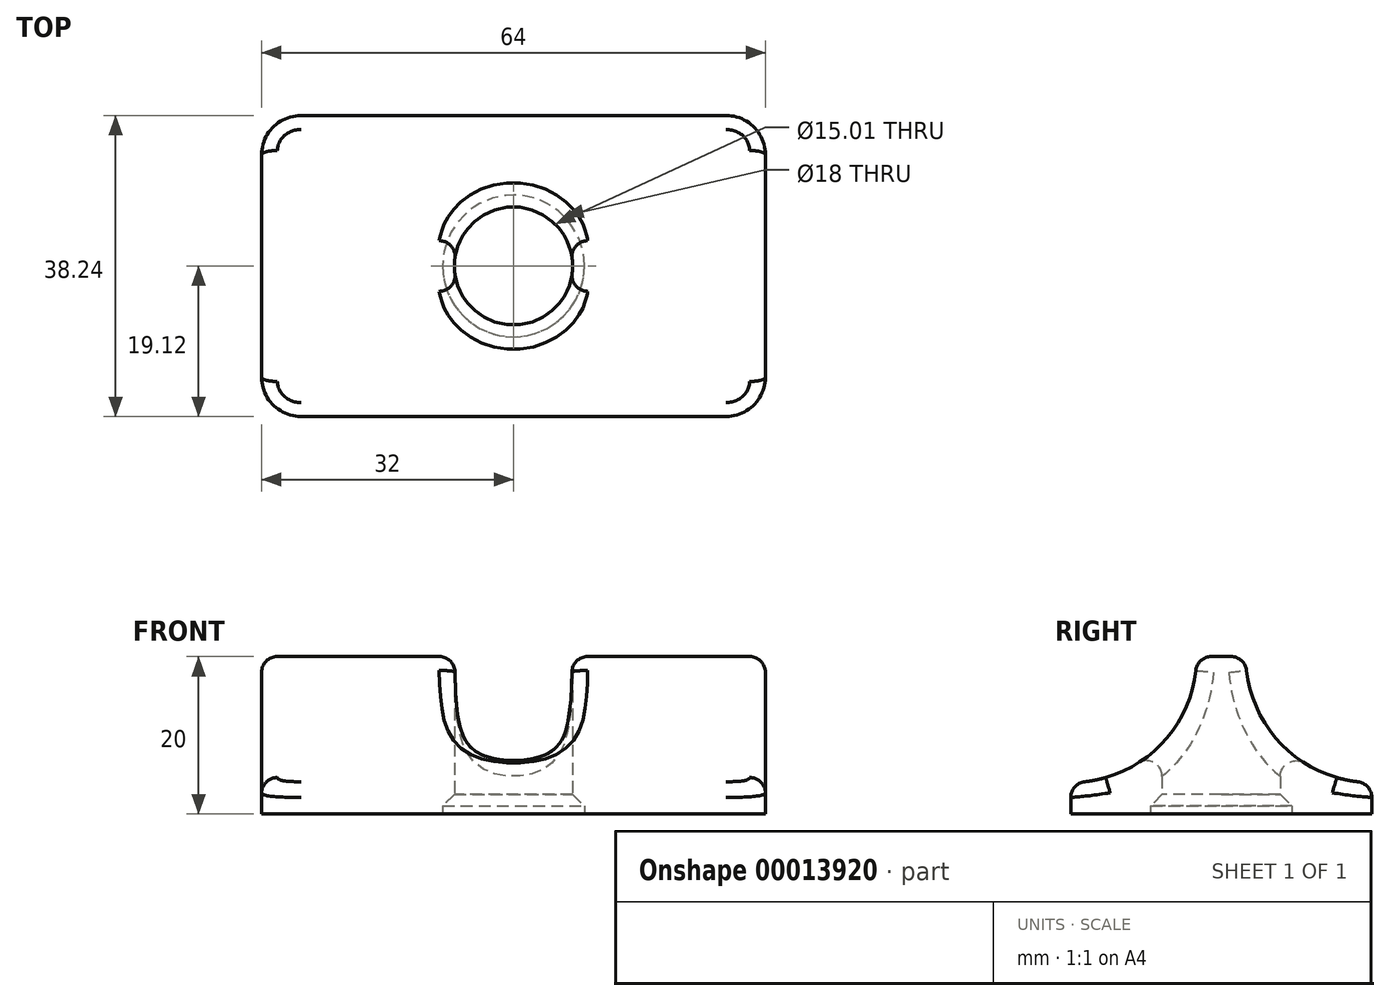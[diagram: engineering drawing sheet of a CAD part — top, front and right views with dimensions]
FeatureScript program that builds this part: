
annotation { "Feature Type Name" : "Feature", "Feature Type Description" : "" }
export const myFeature = defineFeature(function(context is Context, id is Id, definition is map)
    precondition{}
    {
        {
            var Q0;
            Q0=qCreatedBy(makeId("Right.planeOp"),FACE);
            var sketch = newSketch(context, id + "F0", { "sketchPlane" : qUnion([Q0])});
            skLineSegment(sketch, "E0", {"start": v(-19.12, 0) * mm, "end": v(19.12, 0) * mm});
            skArc(sketch, "E1", {"start": v(3.12, 20) * mm, "mid": v(7.8, 8.69) * mm, "end": v(19.12, 4) * mm});
            skArc(sketch, "E2", {"start": v(-19.12, 4) * mm, "mid": v(-7.8, 8.69) * mm, "end": v(-3.12, 20) * mm});
            skLineSegment(sketch, "E3", {"start": v(-19.12, 0) * mm, "end": v(-19.12, 4) * mm});
            skLineSegment(sketch, "E4", {"start": v(19.12, 0) * mm, "end": v(19.12, 4) * mm});
            skLineSegment(sketch, "E5", {"start": v(-7.5, 0) * mm, "end": v(-7.5, 9) * mm, "construction": true});
            skLineSegment(sketch, "E6", {"start": v(-7.5, 9) * mm, "end": v(7.5, 9) * mm, "construction": true});
            skLineSegment(sketch, "E7", {"start": v(7.5, 9) * mm, "end": v(7.5, 0) * mm, "construction": true});
            skLineSegment(sketch, "E8", {"start": v(0, 9) * mm, "end": v(0, 0) * mm, "construction": true});
            skLineSegment(sketch, "E9", {"start": v(-3.12, 20) * mm, "end": v(3.12, 20) * mm});
            skSolve(sketch);
        }
        {
            var Q0;
            Q0=makeQuery(id+"F0.imprint","IMPRINT",FACE,{"disambiguationData":[TD([[makeQuery(id+"F0.imprint","IMPRINT",EDGE,{"derivedFrom":sQuery(id+"F0.wireOp",EDGE,"E0")}),1.0]])]});
            extrude(context, id + "F1", {"entities" : qUnion([Q0]), "flatOperationType" : FlatOperationType.REMOVE, "depth" : 64 * mm, "offsetDistance" : 25 * mm, "domain" : OperationDomain.MODEL, "symmetric" : true});
        }
        {
            var Q0;
            Q0=qCreatedBy(makeId("Top.planeOp"),FACE);
            var sketch = newSketch(context, id + "F2", { "sketchPlane" : qUnion([Q0])});
            skCircle(sketch, "E10.cCircle", {"center": v(0, 0) * mm, "radius": 7.5 * mm});
            skLineSegment(sketch, "E10.0", {"start": v(6.5, 3.75) * mm, "end": v(6.5, -3.75) * mm, "construction": true});
            skLineSegment(sketch, "E10.1", {"start": v(6.5, -3.75) * mm, "end": v(0, -7.5) * mm, "construction": true});
            skLineSegment(sketch, "E10.2", {"start": v(0, -7.5) * mm, "end": v(-6.5, -3.75) * mm, "construction": true});
            skLineSegment(sketch, "E10.3", {"start": v(-6.5, -3.75) * mm, "end": v(-6.5, 3.75) * mm, "construction": true});
            skLineSegment(sketch, "E10.4", {"start": v(-6.5, 3.75) * mm, "end": v(0, 7.5) * mm, "construction": true});
            skLineSegment(sketch, "E10.5", {"start": v(0, 7.5) * mm, "end": v(6.5, 3.75) * mm, "construction": true});
            skSolve(sketch);
        }
        {
            var Q0;
            Q0=qSketchRegion(id+"F2",true);
            extrude(context, id + "F3", {"entities" : qUnion([Q0]), "operationType" : NewBodyOperationType.REMOVE, "endBound" : BoundingType.THROUGH_ALL, "depth" : 10 * mm});
        }
        {
            var Q0;
            {var subQ0=sQuery(id+"F0.wireOp",EDGE,"E9");var subQ1=sQuery(id+"F0.wireOp",EDGE,"E2");var subQ2=sQuery(id+"F0.wireOp",EDGE,"E1");Q0=makeQuery(id+"F3.boolean.opBoolean","SPLIT",FACE,{"disambiguationData":[TD([makeQuery(id+"F1.opExtrude","CAP_FACE",FACE,{"disambiguationData":[OSD([sQuery(id+"F0.wireOp",EDGE,"E0"),subQ2,subQ1,sQuery(id+"F0.wireOp",EDGE,"E3"),sQuery(id+"F0.wireOp",EDGE,"E4"),subQ0])],"isStart":true})])],"derivedFrom":makeQuery(id+"F1.opExtrude","SWEPT_FACE",FACE,{"disambiguationData":[OSD([subQ0])]})});}
            var Q1;
            {var subQ0=sQuery(id+"F0.wireOp",EDGE,"E9");var subQ1=sQuery(id+"F0.wireOp",EDGE,"E2");var subQ2=sQuery(id+"F0.wireOp",EDGE,"E1");Q1=makeQuery(id+"F3.boolean.opBoolean","SPLIT",FACE,{"disambiguationData":[TD([makeQuery(id+"F1.opExtrude","CAP_FACE",FACE,{"disambiguationData":[OSD([sQuery(id+"F0.wireOp",EDGE,"E0"),subQ2,subQ1,sQuery(id+"F0.wireOp",EDGE,"E3"),sQuery(id+"F0.wireOp",EDGE,"E4"),subQ0])],"isStart":false})])],"derivedFrom":makeQuery(id+"F1.opExtrude","SWEPT_FACE",FACE,{"disambiguationData":[OSD([subQ0])]})});}
            var Q2;
            Q2=makeQuery(id+"F1.opExtrude","SWEPT_FACE",FACE,{"disambiguationData":[OSD([sQuery(id+"F0.wireOp",EDGE,"E2")])]});
            var Q3;
            Q3=makeQuery(id+"F1.opExtrude","SWEPT_FACE",FACE,{"disambiguationData":[OSD([sQuery(id+"F0.wireOp",EDGE,"E1")])]});
            fillet(context, id + "F4", {"entities" : qUnion([Q0, Q1, Q2, Q3]), "radius" : 2 * mm, "tangentPropagation" : true, "allowEdgeOverflow" : false});
        }
        {
            var Q0;
            Q0=makeQuery(id+"F1.opExtrude","CAP_EDGE",EDGE,{"disambiguationData":[OSD([sQuery(id+"F0.wireOp",EDGE,"E3")])],"isStart":false});
            var Q1;
            Q1=makeQuery(id+"F1.opExtrude","CAP_EDGE",EDGE,{"disambiguationData":[OSD([sQuery(id+"F0.wireOp",EDGE,"E4")])],"isStart":false});
            var Q2;
            Q2=makeQuery(id+"F1.opExtrude","CAP_EDGE",EDGE,{"disambiguationData":[OSD([sQuery(id+"F0.wireOp",EDGE,"E3")])],"isStart":true});
            var Q3;
            Q3=makeQuery(id+"F1.opExtrude","CAP_EDGE",EDGE,{"disambiguationData":[OSD([sQuery(id+"F0.wireOp",EDGE,"E4")])],"isStart":true});
            fillet(context, id + "F5", {"entities" : qUnion([Q0, Q1, Q2, Q3]), "radius" : 5 * mm, "tangentPropagation" : true, "allowEdgeOverflow" : false});
        }
        {
            var Q0;
            Q0=qCreatedBy(makeId("Top.planeOp"),FACE);
            var sketch = newSketch(context, id + "F6", { "sketchPlane" : qUnion([Q0])});
            skCircle(sketch, "E11", {"center": v(0, 0) * mm, "radius": 9 * mm});
            skSolve(sketch);
        }
        {
            var Q0;
            Q0=qSketchRegion(id+"F6",true);
            extrude(context, id + "F7", {"entities" : qUnion([Q0]), "operationType" : NewBodyOperationType.REMOVE, "depth" : 1 * mm});
        }
        {
            var Q0;
            Q0=makeQuery(id+"F7.boolean.opBoolean","INTERSECT",EDGE,{"derivedFrom":[makeQuery(id+"F3.boolean.opBoolean","COPY",FACE,{"derivedFrom":makeQuery(id+"F3.opExtrude","SWEPT_FACE",FACE,{"disambiguationData":[OSD([sQuery(id+"F2.wireOp",EDGE,"E10.cCircle")])]})}),makeQuery(id+"F7.opExtrude","CAP_FACE",FACE,{"disambiguationData":[OSD([sQuery(id+"F6.wireOp",EDGE,"E11")])],"isStart":false})]});
            chamfer(context, id + "F8", {"entities" : qUnion([Q0]), "width" : 1.5 * mm, "tangentPropagation" : true});
        }
    });
